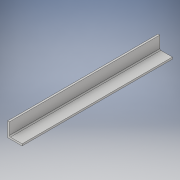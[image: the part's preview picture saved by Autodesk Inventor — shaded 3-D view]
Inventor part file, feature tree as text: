
AUTODESK INVENTOR PART (.ipt)
format: ipt  version: 2017 (Build 210142000, 142)  size: 99,328 bytes
history: native  units: in
note: dims shown in document units (in); Inventor stores cm internally (conversion verified against a paired STEP export)
features: extrude x1, sketch x1
ambient origin geometry x8: Origin, YZ Plane, XZ Plane, XY Plane, X Axis, Y Axis, Z Axis, Center Point
bodies: Solid1 (feature_tree)
feature tree (2):
  extrude  "Extrusion1"  Depth=1.0in
  sketch  "Sketch1"  dims[d4=10.375in d5=0.0in d6=1.0in d7=1.0in]
